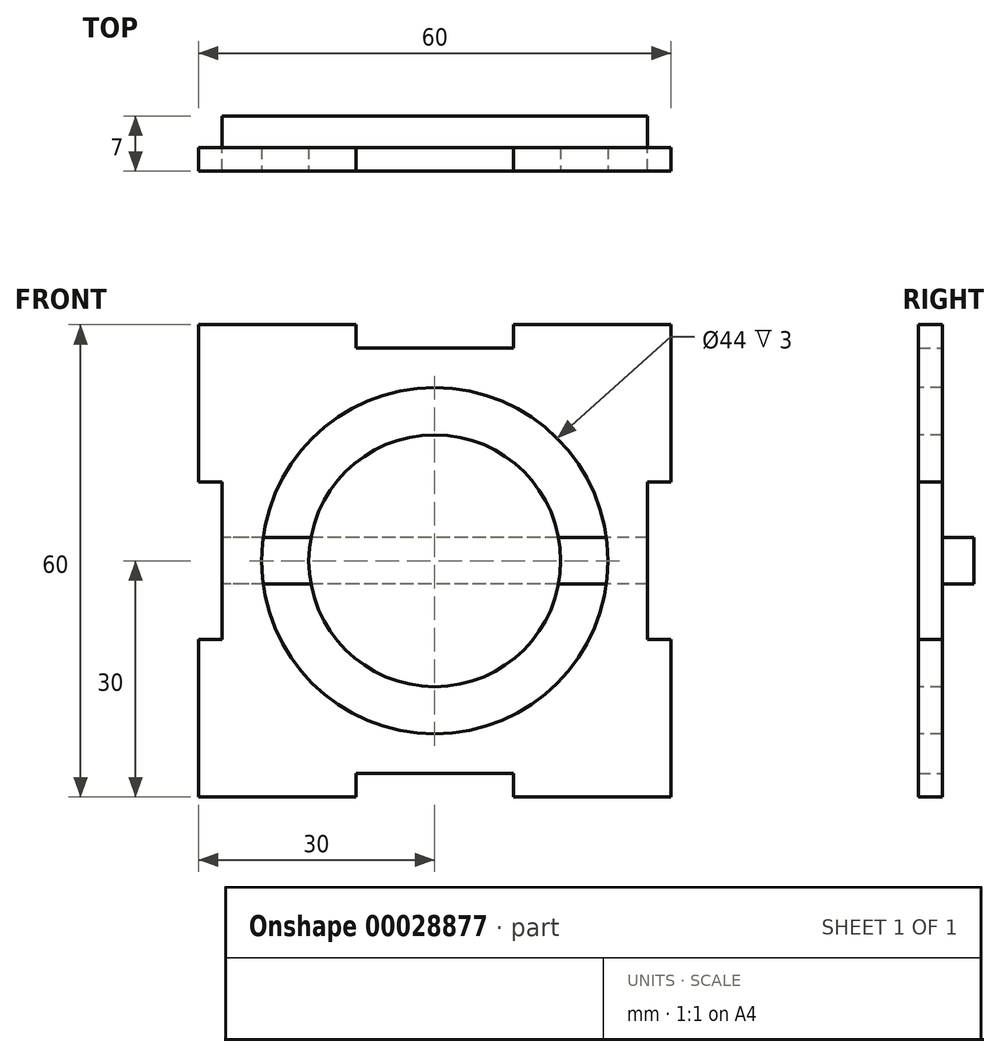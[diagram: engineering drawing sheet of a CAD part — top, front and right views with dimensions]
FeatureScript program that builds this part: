
annotation { "Feature Type Name" : "Feature", "Feature Type Description" : "" }
export const myFeature = defineFeature(function(context is Context, id is Id, definition is map)
    precondition{}
    {
        {
            var Q0;
            Q0=qCreatedBy(makeId("Front.planeOp"),FACE);
            var sketch = newSketch(context, id + "F0", { "sketchPlane" : qUnion([Q0])});
            skLineSegment(sketch, "E0", {"start": v(0, 27) * mm, "end": v(-10, 27) * mm});
            skLineSegment(sketch, "E1", {"start": v(-10, 27) * mm, "end": v(-10, 30) * mm});
            skLineSegment(sketch, "E2", {"start": v(-10, 30) * mm, "end": v(-30, 30) * mm});
            skLineSegment(sketch, "E3", {"start": v(-30, 30) * mm, "end": v(-30, 10) * mm});
            skLineSegment(sketch, "E4", {"start": v(-30, 10) * mm, "end": v(-27, 10) * mm});
            skLineSegment(sketch, "E5", {"start": v(-27, 10) * mm, "end": v(-27, 0) * mm});
            skLineSegment(sketch, "E6.MirrorCS", {"start": v(30, 10) * mm, "end": v(27, 10) * mm});
            skLineSegment(sketch, "E7.MirrorCS", {"start": v(10, 27) * mm, "end": v(10, 30) * mm});
            skLineSegment(sketch, "E8.MirrorCS", {"start": v(27, 10) * mm, "end": v(27, 0) * mm});
            skLineSegment(sketch, "E9.MirrorCS", {"start": v(0, 27) * mm, "end": v(10, 27) * mm});
            skLineSegment(sketch, "E10.MirrorCS", {"start": v(30, 30) * mm, "end": v(30, 10) * mm});
            skLineSegment(sketch, "E11.MirrorCS", {"start": v(10, 30) * mm, "end": v(30, 30) * mm});
            skLineSegment(sketch, "E12.MirrorCS", {"start": v(-10, -27) * mm, "end": v(-10, -30) * mm});
            skLineSegment(sketch, "E13.MirrorCS", {"start": v(30, -10) * mm, "end": v(27, -10) * mm});
            skLineSegment(sketch, "E14.MirrorCS", {"start": v(10, -27) * mm, "end": v(10, -30) * mm});
            skLineSegment(sketch, "E15.MirrorCS", {"start": v(-30, -10) * mm, "end": v(-27, -10) * mm});
            skLineSegment(sketch, "E16.MirrorCS", {"start": v(30, -30) * mm, "end": v(30, -10) * mm});
            skLineSegment(sketch, "E17.MirrorCS", {"start": v(-27, -10) * mm, "end": v(-27, 0) * mm});
            skLineSegment(sketch, "E18.MirrorCS", {"start": v(0, -27) * mm, "end": v(-10, -27) * mm});
            skLineSegment(sketch, "E19.MirrorCS", {"start": v(10, -30) * mm, "end": v(30, -30) * mm});
            skLineSegment(sketch, "E20.MirrorCS", {"start": v(-10, -30) * mm, "end": v(-30, -30) * mm});
            skLineSegment(sketch, "E21.MirrorCS", {"start": v(-30, -30) * mm, "end": v(-30, -10) * mm});
            skLineSegment(sketch, "E22.MirrorCS", {"start": v(0, -27) * mm, "end": v(10, -27) * mm});
            skLineSegment(sketch, "E23.MirrorCS", {"start": v(27, -10) * mm, "end": v(27, 0) * mm});
            skSolve(sketch);
        }
        {
            var Q0;
            Q0=makeQuery(id+"F0.imprint","IMPRINT",FACE,{"disambiguationData":[TD([[makeQuery(id+"F0.imprint","IMPRINT",EDGE,{"derivedFrom":sQuery(id+"F0.wireOp",EDGE,"E4")}),1.0]])]});
            extrude(context, id + "F1", {"entities" : qUnion([Q0]), "depth" : 3 * mm});
        }
        {
            var Q0;
            Q0=makeQuery(id+"F1.opExtrude","CAP_FACE",FACE,{"disambiguationData":[OSD([sQuery(id+"F0.wireOp",EDGE,"E4"),sQuery(id+"F0.wireOp",EDGE,"E1"),sQuery(id+"F0.wireOp",EDGE,"E6.MirrorCS"),sQuery(id+"F0.wireOp",EDGE,"E7.MirrorCS"),sQuery(id+"F0.wireOp",EDGE,"E11.MirrorCS"),sQuery(id+"F0.wireOp",EDGE,"E10.MirrorCS"),sQuery(id+"F0.wireOp",EDGE,"E9.MirrorCS"),sQuery(id+"F0.wireOp",EDGE,"E8.MirrorCS"),sQuery(id+"F0.wireOp",EDGE,"E2"),sQuery(id+"F0.wireOp",EDGE,"E5"),sQuery(id+"F0.wireOp",EDGE,"E3"),sQuery(id+"F0.wireOp",EDGE,"E0"),sQuery(id+"F0.wireOp",EDGE,"E12.MirrorCS"),sQuery(id+"F0.wireOp",EDGE,"E14.MirrorCS"),sQuery(id+"F0.wireOp",EDGE,"E13.MirrorCS"),sQuery(id+"F0.wireOp",EDGE,"E15.MirrorCS"),sQuery(id+"F0.wireOp",EDGE,"E20.MirrorCS"),sQuery(id+"F0.wireOp",EDGE,"E18.MirrorCS"),sQuery(id+"F0.wireOp",EDGE,"E22.MirrorCS"),sQuery(id+"F0.wireOp",EDGE,"E17.MirrorCS"),sQuery(id+"F0.wireOp",EDGE,"E19.MirrorCS"),sQuery(id+"F0.wireOp",EDGE,"E23.MirrorCS"),sQuery(id+"F0.wireOp",EDGE,"E16.MirrorCS"),sQuery(id+"F0.wireOp",EDGE,"E21.MirrorCS")])],"isStart":false});
            var sketch = newSketch(context, id + "F2", { "sketchPlane" : qUnion([Q0])});
            skCircle(sketch, "E24", {"center": v(0, 0) * mm, "radius": 22 * mm});
            skCircle(sketch, "E25", {"center": v(0, 0) * mm, "radius": 16 * mm});
            skSolve(sketch);
        }
        {
            var Q0;
            Q0=makeQuery(id+"F2.imprint","IMPRINT",FACE,{"disambiguationData":[TD([[makeQuery(id+"F2.imprint","IMPRINT",EDGE,{"derivedFrom":sQuery(id+"F2.wireOp",EDGE,"E24")}),1.0]])]});
            extrude(context, id + "F3", {"entities" : qUnion([Q0]), "operationType" : NewBodyOperationType.REMOVE, "oppositeDirection" : true, "depth" : 25 * mm});
        }
        {
            var Q0;
            {var subQ0=sQuery(id+"F0.wireOp",EDGE,"E4");var subQ1=sQuery(id+"F0.wireOp",EDGE,"E1");var subQ2=sQuery(id+"F0.wireOp",EDGE,"E6.MirrorCS");var subQ3=sQuery(id+"F0.wireOp",EDGE,"E7.MirrorCS");var subQ4=sQuery(id+"F0.wireOp",EDGE,"E11.MirrorCS");var subQ5=sQuery(id+"F0.wireOp",EDGE,"E10.MirrorCS");var subQ6=sQuery(id+"F0.wireOp",EDGE,"E9.MirrorCS");var subQ7=sQuery(id+"F0.wireOp",EDGE,"E8.MirrorCS");var subQ8=sQuery(id+"F0.wireOp",EDGE,"E2");var subQ9=sQuery(id+"F0.wireOp",EDGE,"E5");var subQ10=sQuery(id+"F0.wireOp",EDGE,"E3");var subQ11=sQuery(id+"F0.wireOp",EDGE,"E0");var subQ12=sQuery(id+"F0.wireOp",EDGE,"E12.MirrorCS");var subQ13=sQuery(id+"F0.wireOp",EDGE,"E14.MirrorCS");var subQ14=sQuery(id+"F0.wireOp",EDGE,"E13.MirrorCS");var subQ15=sQuery(id+"F0.wireOp",EDGE,"E15.MirrorCS");var subQ16=sQuery(id+"F0.wireOp",EDGE,"E20.MirrorCS");var subQ17=sQuery(id+"F0.wireOp",EDGE,"E18.MirrorCS");var subQ18=sQuery(id+"F0.wireOp",EDGE,"E22.MirrorCS");var subQ19=sQuery(id+"F0.wireOp",EDGE,"E17.MirrorCS");var subQ20=sQuery(id+"F0.wireOp",EDGE,"E19.MirrorCS");var subQ21=sQuery(id+"F0.wireOp",EDGE,"E23.MirrorCS");var subQ22=sQuery(id+"F0.wireOp",EDGE,"E16.MirrorCS");var subQ23=sQuery(id+"F0.wireOp",EDGE,"E21.MirrorCS");Q0=makeQuery(id+"F3.boolean.opBoolean","SPLIT",FACE,{"disambiguationData":[TD([makeQuery(id+"F1.opExtrude","SWEPT_FACE",FACE,{"disambiguationData":[OSD([subQ0])]})])],"derivedFrom":makeQuery(id+"F1.opExtrude","CAP_FACE",FACE,{"disambiguationData":[OSD([subQ0,subQ1,subQ2,subQ3,subQ4,subQ5,subQ6,subQ7,subQ8,subQ9,subQ10,subQ11,subQ12,subQ13,subQ14,subQ15,subQ16,subQ17,subQ18,subQ19,subQ20,subQ21,subQ22,subQ23])],"isStart":true})});}
            var sketch = newSketch(context, id + "F4", { "sketchPlane" : qUnion([Q0])});
            skLineSegment(sketch, "E26.rect.bottom", {"start": v(-27, -2.97) * mm, "end": v(27, -2.97) * mm});
            skLineSegment(sketch, "E26.rect.top", {"start": v(-27, 2.97) * mm, "end": v(27, 2.97) * mm});
            skLineSegment(sketch, "E26.rect.left", {"start": v(-27, -2.97) * mm, "end": v(-27, 2.97) * mm});
            skLineSegment(sketch, "E26.rect.right", {"start": v(27, -2.97) * mm, "end": v(27, 2.97) * mm});
            skPoint(sketch, "E26.rect.middle", {"position": v(0, 0) * mm});
            skSolve(sketch);
        }
        {
            var Q0;
            {var subQ0=makeQuery(id+"F3.boolean.opBoolean","INTERSECT",EDGE,{"derivedFrom":[makeQuery(id+"F1.opExtrude","CAP_FACE",FACE,{"disambiguationData":[OSD([sQuery(id+"F0.wireOp",EDGE,"E4"),sQuery(id+"F0.wireOp",EDGE,"E1"),sQuery(id+"F0.wireOp",EDGE,"E6.MirrorCS"),sQuery(id+"F0.wireOp",EDGE,"E7.MirrorCS"),sQuery(id+"F0.wireOp",EDGE,"E11.MirrorCS"),sQuery(id+"F0.wireOp",EDGE,"E10.MirrorCS"),sQuery(id+"F0.wireOp",EDGE,"E9.MirrorCS"),sQuery(id+"F0.wireOp",EDGE,"E8.MirrorCS"),sQuery(id+"F0.wireOp",EDGE,"E2"),sQuery(id+"F0.wireOp",EDGE,"E5"),sQuery(id+"F0.wireOp",EDGE,"E3"),sQuery(id+"F0.wireOp",EDGE,"E0"),sQuery(id+"F0.wireOp",EDGE,"E12.MirrorCS"),sQuery(id+"F0.wireOp",EDGE,"E14.MirrorCS"),sQuery(id+"F0.wireOp",EDGE,"E13.MirrorCS"),sQuery(id+"F0.wireOp",EDGE,"E15.MirrorCS"),sQuery(id+"F0.wireOp",EDGE,"E20.MirrorCS"),sQuery(id+"F0.wireOp",EDGE,"E18.MirrorCS"),sQuery(id+"F0.wireOp",EDGE,"E22.MirrorCS"),sQuery(id+"F0.wireOp",EDGE,"E17.MirrorCS"),sQuery(id+"F0.wireOp",EDGE,"E19.MirrorCS"),sQuery(id+"F0.wireOp",EDGE,"E23.MirrorCS"),sQuery(id+"F0.wireOp",EDGE,"E16.MirrorCS"),sQuery(id+"F0.wireOp",EDGE,"E21.MirrorCS")])],"isStart":true}),makeQuery(id+"F3.opExtrude","SWEPT_FACE",FACE,{"disambiguationData":[OSD([sQuery(id+"F2.wireOp",EDGE,"E24")])]})]});var subQ3=sQuery(id+"F4.wireOp",EDGE,"E26.rect.bottom");var subQ6=makeQuery(id+"F4.imprint","INTERSECT",VERTEX,{"disambiguationData":[OD(0.0)],"derivedFrom":[subQ0,subQ3]});Q0=makeQuery(id+"F4.imprint","IMPRINT",FACE,{"disambiguationData":[TD([[makeQuery(id+"F4.imprint","IMPRINT",EDGE,{"disambiguationData":[TD([[subQ6,-1.0]])],"derivedFrom":subQ3}),1.0]])]});}
            var Q1;
            {var subQ7=sQuery(id+"F4.wireOp",EDGE,"E26.rect.left");Q1=makeQuery(id+"F4.imprint","IMPRINT",FACE,{"disambiguationData":[TD([[makeQuery(id+"F4.imprint","IMPRINT",EDGE,{"derivedFrom":subQ7}),-1.0]])]});}
            var Q2;
            {var subQ0=sQuery(id+"F4.wireOp",EDGE,"E26.rect.right");Q2=makeQuery(id+"F4.imprint","IMPRINT",FACE,{"disambiguationData":[TD([[makeQuery(id+"F4.imprint","IMPRINT",EDGE,{"derivedFrom":subQ0}),-1.0]])]});}
            extrude(context, id + "F5", {"entities" : qUnion([Q0, Q1, Q2]), "depth" : 4 * mm});
        }
    });
